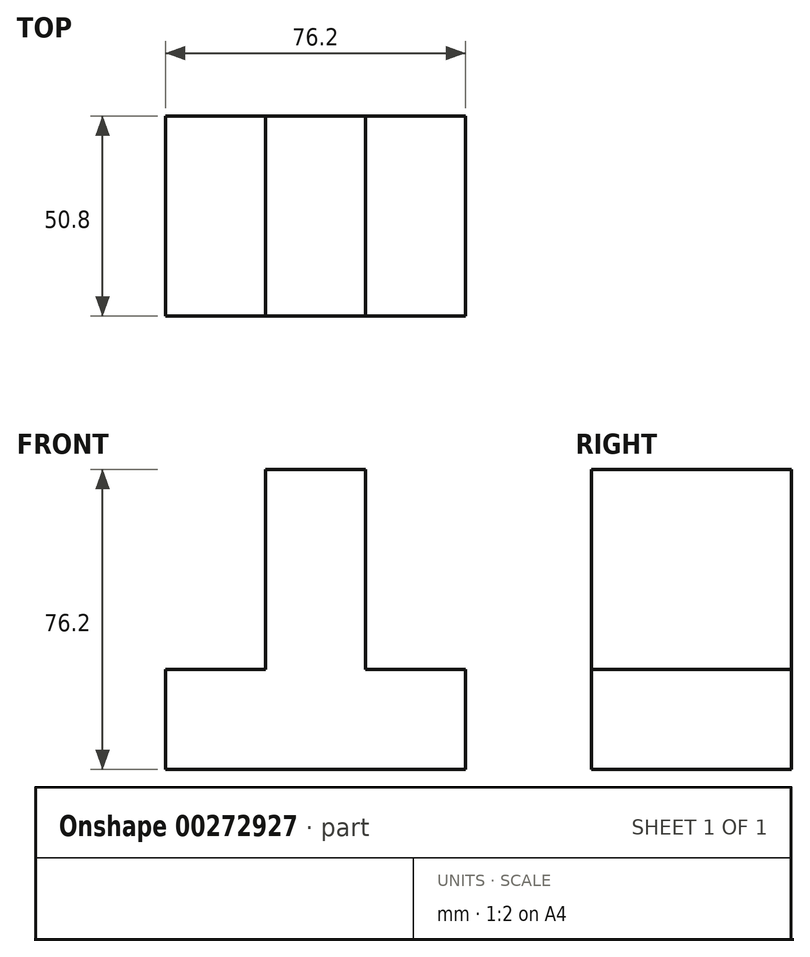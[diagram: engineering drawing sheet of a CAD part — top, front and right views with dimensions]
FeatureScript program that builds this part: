
annotation { "Feature Type Name" : "Feature", "Feature Type Description" : "" }
export const myFeature = defineFeature(function(context is Context, id is Id, definition is map)
    precondition{}
    {
        {
            var Q0;
            Q0=qCreatedBy(makeId("Front.planeOp"),FACE);
            var sketch = newSketch(context, id + "F0", { "sketchPlane" : qUnion([Q0])});
            skLineSegment(sketch, "E0", {"start": v(0, 0) * mm, "end": v(-76.2, 0) * mm});
            skLineSegment(sketch, "E1", {"start": v(-76.2, 0) * mm, "end": v(-76.2, 25.4) * mm});
            skLineSegment(sketch, "E2", {"start": v(-76.2, 25.4) * mm, "end": v(-50.8, 25.4) * mm});
            skLineSegment(sketch, "E3", {"start": v(-50.8, 25.4) * mm, "end": v(-50.8, 76.2) * mm});
            skLineSegment(sketch, "E4", {"start": v(-50.8, 76.2) * mm, "end": v(-25.4, 76.2) * mm});
            skLineSegment(sketch, "E5", {"start": v(-25.4, 76.2) * mm, "end": v(-25.4, 25.4) * mm});
            skLineSegment(sketch, "E6", {"start": v(-25.4, 25.4) * mm, "end": v(0, 25.4) * mm});
            skLineSegment(sketch, "E7", {"start": v(0, 25.4) * mm, "end": v(0, 0) * mm});
            skSolve(sketch);
        }
        {
            var Q0;
            Q0=makeQuery(id+"F0.imprint","IMPRINT",FACE,{"disambiguationData":[TD([[makeQuery(id+"F0.imprint","IMPRINT",EDGE,{"derivedFrom":sQuery(id+"F0.wireOp",EDGE,"E0")}),-1.0]])]});
            extrude(context, id + "F1", {"entities" : qUnion([Q0]), "depth" : 50.8 * mm});
        }
    });
